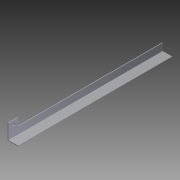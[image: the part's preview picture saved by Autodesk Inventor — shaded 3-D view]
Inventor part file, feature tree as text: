
AUTODESK INVENTOR PART (.ipt)
format: ipt  version: 2012 (Build 160160000, 160)  size: 77,312 bytes
history: native  units: in
note: dims shown in document units (in); Inventor stores cm internally (conversion verified against a paired STEP export)
features: other x3, sketch x1
ambient origin geometry x8: Origin, YZ Plane, XZ Plane, XY Plane, X Axis, Y Axis, Z Axis, Center Point
bodies: Solid1 (feature_tree)
feature tree (4):
  other  "8 ball top roller L frame.ipt"
  other  "Solid1::8 ball top roller L frame.ipt"
  sketch  "Sketch1"  dims[d0=0.3937in]
  other  "TaggingFeature1"
